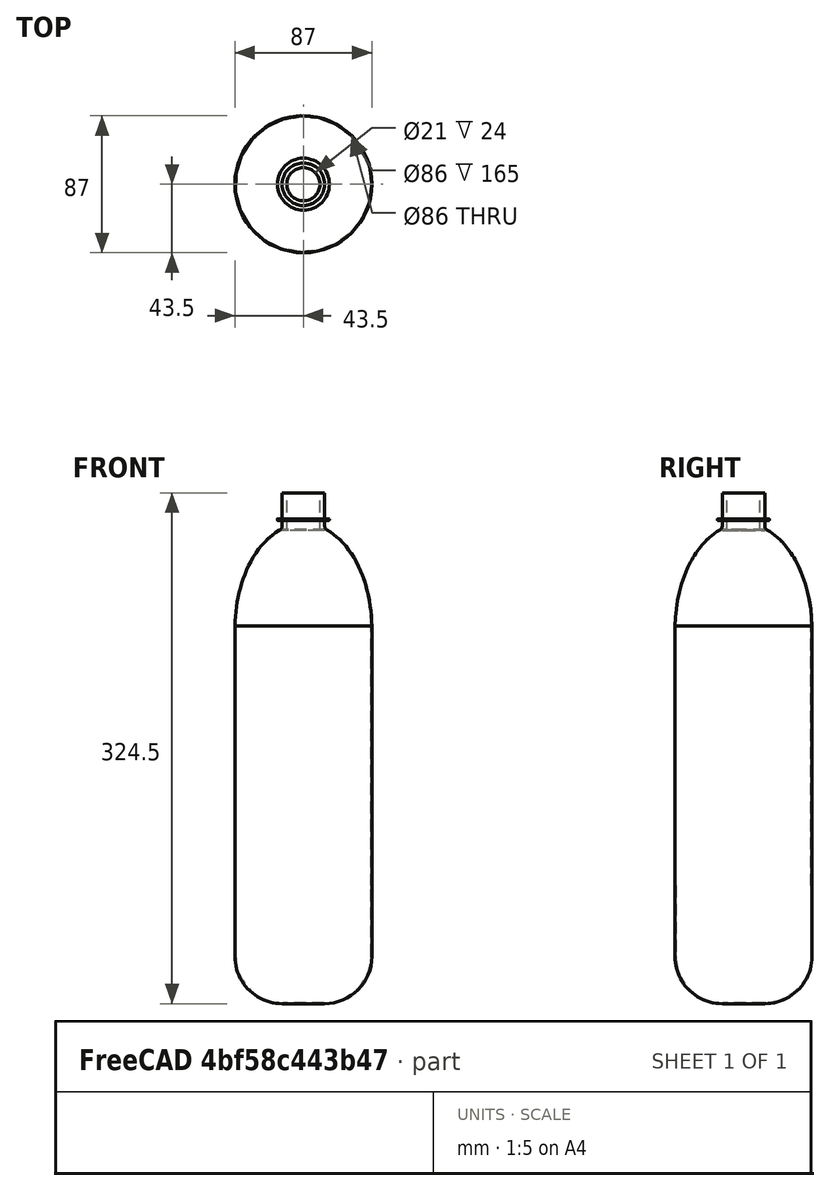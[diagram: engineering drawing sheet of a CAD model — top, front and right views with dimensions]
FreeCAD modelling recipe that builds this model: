
FCSTD DOCUMENT  (FreeCAD 1.0R39109 (Git))
Label: Botella
License: All rights reserved
LicenseURL: http://en.wikipedia.org/wiki/All_rights_reserved
objects: Part::Cut×4, Part::MultiFuse×4, Part::Fillet×4, Part::FeaturePython×3, Part::Cylinder×3, Part::Ellipsoid×2, Part::Box×1
note: 21 computed .brp shape members not serialized (recipe doc carries the construction recipe); baked Part::Feature solids carry a one-line shape summary decoded from their .brp

FEATURE [Part::FeaturePython] Tube  # WARN: FeaturePython — macro-defined, semantics opaque (R4)
  AttacherType = Attacher::AttachEngine3D
  Height = 165
  InnerRadius = 43
  OuterRadius = 43.5
  Placement = pos=(0,0,-17) rot=(0,0,1;0rad)
FEATURE [Part::Ellipsoid] Ellipsoid  label="Elipsoide"
  Angle1 = -90
  Angle2 = 90
  Angle3 = 360
  AttacherType = Attacher::AttachEngine3D
  Placement = pos=(0,0,146) rot=(0,0,1;0rad)
  Radius1 = 67
  Radius2 = 43.5
  Radius3 = 43.5
FEATURE [Part::Ellipsoid] Ellipsoid001  label="Elipsoide001"
  Angle1 = -90
  Angle2 = 90
  Angle3 = 360
  AttacherType = Attacher::AttachEngine3D
  Placement = pos=(0,0,146) rot=(0,0,1;0rad)
  Radius1 = 66.5
  Radius2 = 43
  Radius3 = 43
FEATURE [Part::Cut] Cut236
  Base = -> Ellipsoid
  Tool = -> Ellipsoid001
FEATURE [Part::Box] Box185  label="Cubo173"
  AttacherType = Attacher::AttachEngine3D
  Height = 120
  Length = 90
  Placement = pos=(-45,-44,28) rot=(0,0,1;0rad)
  Width = 90
FEATURE [Part::Cut] Cut237
  Base = -> Cut236
  Tool = -> Box185
FEATURE [Part::MultiFuse] Fusion110
  Shapes = -> [Cut237,Tube]
FEATURE [Part::Cylinder] Cylinder164  label="Cilindro164"
  Angle = 360
  AttacherType = Attacher::AttachEngine3D
  FirstAngle = 0
  Height = 10
  Placement = pos=(0,0,207) rot=(0,0,1;0rad)
  Radius = 11
  SecondAngle = 0
FEATURE [Part::Cut] Cut238
  Base = -> Fusion110
  Tool = -> Cylinder164
FEATURE [Part::FeaturePython] Tube001  # WARN: FeaturePython — macro-defined, semantics opaque (R4)
  AttacherType = Attacher::AttachEngine3D
  Height = 24
  InnerRadius = 10.5
  OuterRadius = 13.5
  Placement = pos=(0,0,208.5) rot=(0,0,1;0rad)
FEATURE [Part::MultiFuse] Fusion111
  Shapes = -> [Cut238,Tube001]
FEATURE [Part::FeaturePython] Tube002  # WARN: FeaturePython — macro-defined, semantics opaque (R4)
  AttacherType = Attacher::AttachEngine3D
  Height = 1
  InnerRadius = 13.5
  OuterRadius = 16.5
FEATURE [Part::Fillet] Fillet149
  Base = -> Tube002
  EdgeLinks = -> Tube002 [Edge1,Edge3]
  Edges = 2 edges r=0.3: [Edge1,Edge3]
  Placement = pos=(0,0,215) rot=(0,0,1;0rad)
FEATURE [Part::Fillet] Fillet150
  Base = -> Fusion111
  EdgeLinks = -> Fusion111 [Edge2]
  Edges = 1 edges r=3: [Edge2]
FEATURE [Part::MultiFuse] Fusion112  label="Botella"
  Shapes = -> [Fillet149,Fillet150]
FEATURE [Part::Cylinder] Cylinder165  label="Cilindro165"
  Angle = 360
  AttacherType = Attacher::AttachEngine3D
  FirstAngle = 0
  Height = 75
  Placement = pos=(0,0,-98) rot=(0,0,1;0rad)
  Radius = 43.5
  SecondAngle = 0
FEATURE [Part::Fillet] Fillet151
  Base = -> Cylinder165
  EdgeLinks = -> Cylinder165 [Edge2]
  Edges = 1 edges r=30: [Edge2]
FEATURE [Part::Cylinder] Cylinder166  label="Cilindro166"
  Angle = 360
  AttacherType = Attacher::AttachEngine3D
  FirstAngle = 0
  Height = 74.5
  Placement = pos=(0,0,-98) rot=(0,0,1;0rad)
  Radius = 43
  SecondAngle = 0
FEATURE [Part::Fillet] Fillet152
  Base = -> Cylinder166
  EdgeLinks = -> Cylinder166 [Edge2]
  Edges = 1 edges r=30: [Edge2]
  Placement = pos=(0,0,0.5) rot=(0,0,1;0rad)
FEATURE [Part::Cut] Cut239
  Base = -> Fillet151
  Placement = pos=(0,0,6) rot=(0,0,1;0rad)
  Tool = -> Fillet152
FEATURE [Part::MultiFuse] Fusion113  label="Botella_Alteza"
  Shapes = -> [Fusion112,Cut239]
